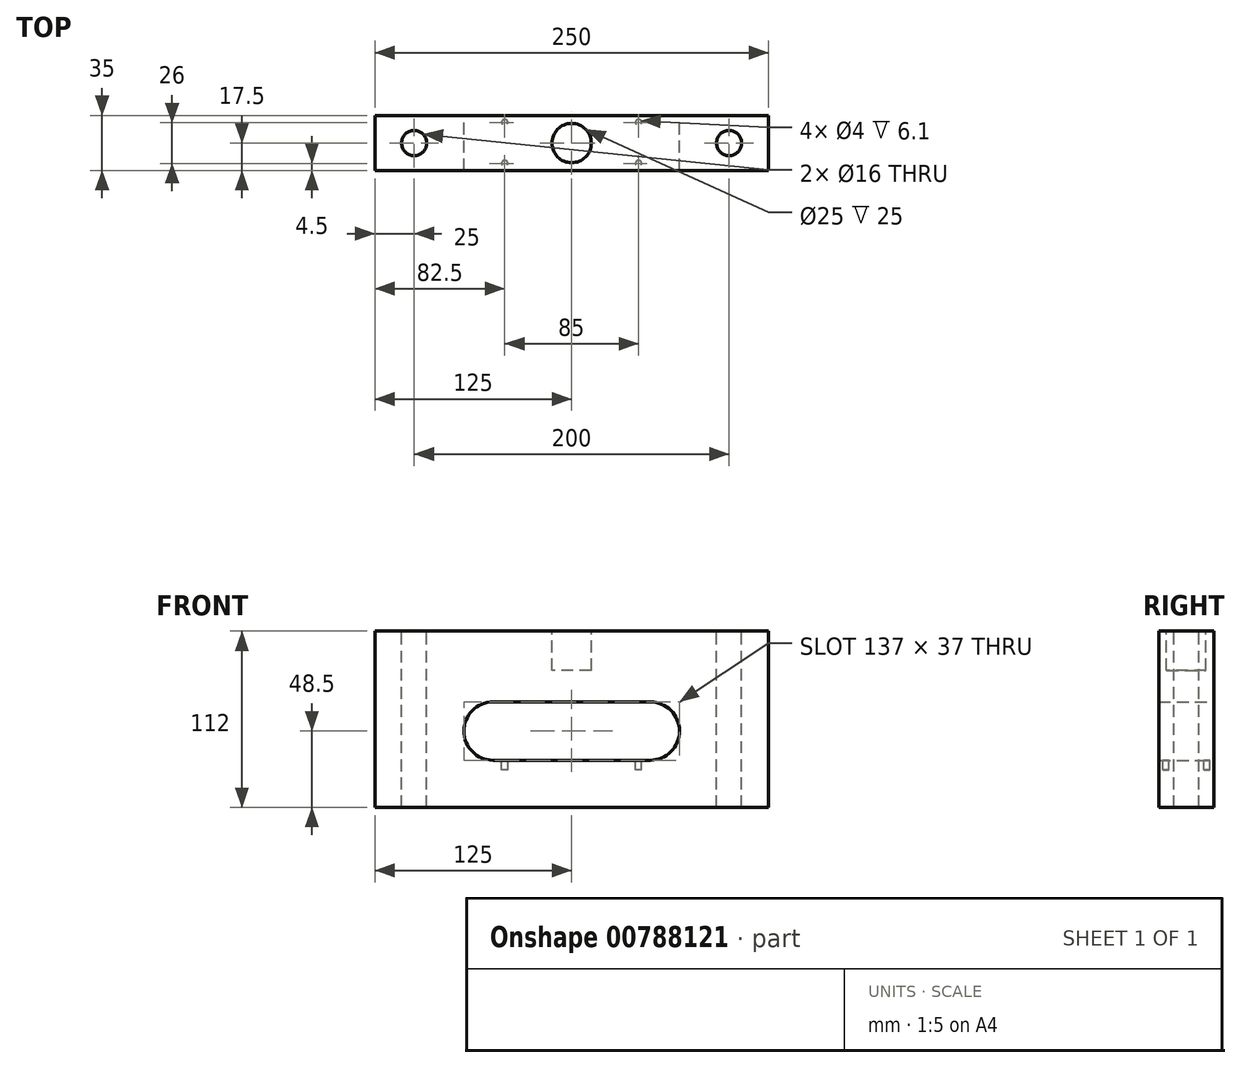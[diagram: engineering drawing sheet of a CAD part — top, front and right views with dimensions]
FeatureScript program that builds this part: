
annotation { "Feature Type Name" : "Feature", "Feature Type Description" : "" }
export const myFeature = defineFeature(function(context is Context, id is Id, definition is map)
    precondition{}
    {
        {
            var Q0;
            Q0=qCreatedBy(makeId("Front.planeOp"),FACE);
            var sketch = newSketch(context, id + "F0", { "sketchPlane" : qUnion([Q0])});
            skLineSegment(sketch, "E0.bottom", {"start": v(-50, -18.5) * mm, "end": v(50, -18.5) * mm});
            skLineSegment(sketch, "E0.top", {"start": v(-50, 18.5) * mm, "end": v(50, 18.5) * mm});
            skLineSegment(sketch, "E0.left", {"start": v(-50, -18.5) * mm, "end": v(-50, 18.5) * mm, "construction": true});
            skLineSegment(sketch, "E0.right", {"start": v(50, -18.5) * mm, "end": v(50, 18.5) * mm, "construction": true});
            skLineSegment(sketch, "E1.bottom", {"start": v(125, 63.5) * mm, "end": v(-125, 63.5) * mm});
            skLineSegment(sketch, "E1.top", {"start": v(125, -48.5) * mm, "end": v(-125, -48.5) * mm});
            skLineSegment(sketch, "E1.left", {"start": v(125, 63.5) * mm, "end": v(125, -48.5) * mm});
            skLineSegment(sketch, "E1.right", {"start": v(-125, 63.5) * mm, "end": v(-125, -48.5) * mm});
            skPoint(sketch, "E2", {"position": v(-50, 0) * mm});
            skPoint(sketch, "E3", {"position": v(0, -18.5) * mm});
            skPoint(sketch, "E4", {"position": v(0, -48.5) * mm});
            skPoint(sketch, "E5", {"position": v(-125, 7.5) * mm});
            skArc(sketch, "E6", {"start": v(-50, 18.5) * mm, "mid": v(-68.5, 0) * mm, "end": v(-50, -18.5) * mm});
            skArc(sketch, "E7", {"start": v(50, -18.5) * mm, "mid": v(68.5, 0) * mm, "end": v(50, 18.5) * mm});
            skSolve(sketch);
        }
        {
            var Q0;
            Q0=qSketchRegion(id+"F0",true);
            extrude(context, id + "F1", {"entities" : qUnion([Q0]), "depth" : 35 * mm, "offsetDistance" : 25 * mm});
        }
        {
            var Q0;
            Q0=makeQuery(id+"F1.opExtrude","SWEPT_FACE",FACE,{"disambiguationData":[OSD([sQuery(id+"F0.wireOp",EDGE,"E1.bottom")])]});
            var sketch = newSketch(context, id + "F2", { "sketchPlane" : qUnion([Q0])});
            skCircle(sketch, "E8", {"center": v(-100, -17.5) * mm, "radius": 8 * mm});
            skCircle(sketch, "E9", {"center": v(100, -17.5) * mm, "radius": 8 * mm});
            skLineSegment(sketch, "E10", {"start": v(-100, -17.5) * mm, "end": v(100, -17.5) * mm, "construction": true});
            skPoint(sketch, "E11", {"position": v(0, -17.5) * mm});
            skSolve(sketch);
        }
        {
            var Q0;
            Q0 = qSketchRegion(id + "F2", true);
            extrude(context, id + "F3", {"entities" : qUnion([Q0]), "operationType" : NewBodyOperationType.REMOVE, "oppositeDirection" : true, "depth" : 400 * mm, "offsetDistance" : 25 * mm});
        }
        {
            var Q0;
            Q0=makeQuery(id+"F1.opExtrude","SWEPT_FACE",FACE,{"disambiguationData":[OSD([sQuery(id+"F0.wireOp",EDGE,"E1.bottom")])]});
            var sketch = newSketch(context, id + "F4", { "sketchPlane" : qUnion([Q0])});
            skCircle(sketch, "E12", {"center": v(0, -17.5) * mm, "radius": 12.5 * mm});
            skSolve(sketch);
        }
        {
            var Q0;
            Q0 = qSketchRegion(id + "F4", true);
            extrude(context, id + "F5", {"entities" : qUnion([Q0]), "operationType" : NewBodyOperationType.REMOVE, "oppositeDirection" : true, "depth" : 25 * mm, "offsetDistance" : 25 * mm});
        }
        {
            var Q0;
            Q0=makeQuery(id+"F1.opExtrude","SWEPT_FACE",FACE,{"disambiguationData":[OSD([sQuery(id+"F0.wireOp",EDGE,"E0.bottom")])]});
            var sketch = newSketch(context, id + "F6", { "sketchPlane" : qUnion([Q0])});
            skCircle(sketch, "E13", {"center": v(-42.5, -4.5) * mm, "radius": 2 * mm});
            skCircle(sketch, "E14", {"center": v(-42.5, -30.5) * mm, "radius": 2 * mm});
            skCircle(sketch, "E15", {"center": v(42.5, -4.5) * mm, "radius": 2 * mm});
            skCircle(sketch, "E16", {"center": v(42.5, -30.5) * mm, "radius": 2 * mm});
            skSolve(sketch);
        }
        {
            var Q0;
            Q0 = qSketchRegion(id + "F6", true);
            extrude(context, id + "F7", {"entities" : qUnion([Q0]), "operationType" : NewBodyOperationType.REMOVE, "oppositeDirection" : true, "depth" : 6.1 * mm, "offsetDistance" : 25 * mm});
        }
    });
